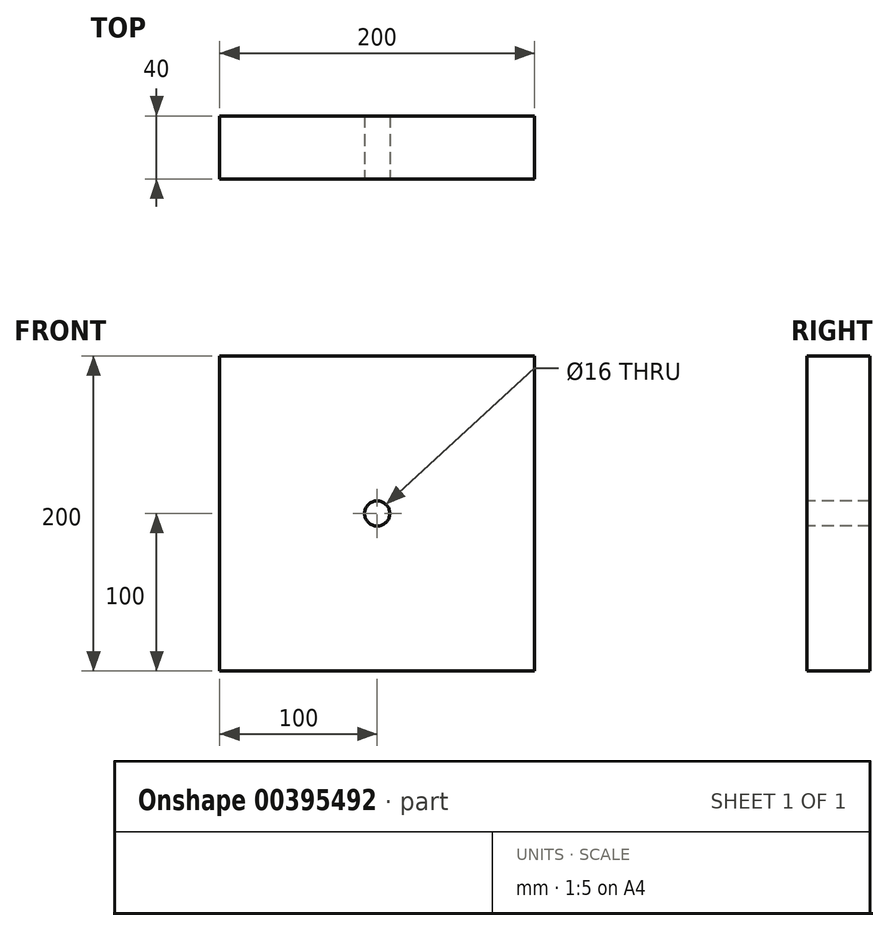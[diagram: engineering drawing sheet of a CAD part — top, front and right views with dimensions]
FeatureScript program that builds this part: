
annotation { "Feature Type Name" : "Feature", "Feature Type Description" : "" }
export const myFeature = defineFeature(function(context is Context, id is Id, definition is map)
    precondition{}
    {
        {
            var Q0;
            Q0=qCreatedBy(makeId("Front.planeOp"),FACE);
            var sketch = newSketch(context, id + "F0", { "sketchPlane" : qUnion([Q0])});
            skLineSegment(sketch, "E0.bottom", {"start": v(-100, 100) * mm, "end": v(100, 100) * mm});
            skLineSegment(sketch, "E0.top", {"start": v(-100, -100) * mm, "end": v(100, -100) * mm});
            skLineSegment(sketch, "E0.left", {"start": v(-100, 100) * mm, "end": v(-100, -100) * mm});
            skLineSegment(sketch, "E0.right", {"start": v(100, 100) * mm, "end": v(100, -100) * mm});
            skCircle(sketch, "E1", {"center": v(0, 0) * mm, "radius": 8 * mm});
            skSolve(sketch);
        }
        {
            var Q0;
            Q0 = qSketchRegion(id + "F0", true);
            extrude(context, id + "F1", {"entities" : qUnion([Q0]), "oppositeDirection" : true, "depth" : 40 * mm});
        }
    });
